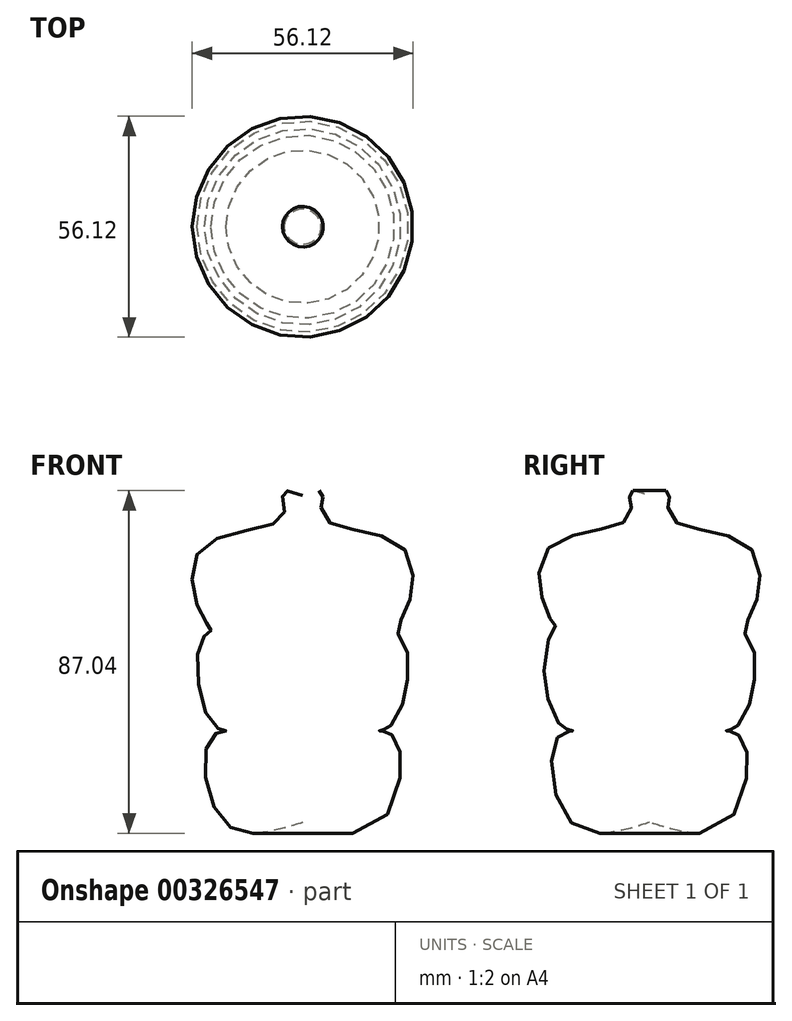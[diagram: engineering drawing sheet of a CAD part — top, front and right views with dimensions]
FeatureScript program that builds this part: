
annotation { "Feature Type Name" : "Feature", "Feature Type Description" : "" }
export const myFeature = defineFeature(function(context is Context, id is Id, definition is map)
    precondition{}
    {
        {
            var Q0;
            Q0=qCreatedBy(makeId("Front.planeOp"),FACE);
            var sketch = newSketch(context, id + "F0", { "sketchPlane" : qUnion([Q0])});
            skLineSegment(sketch, "E0", {"start": v(0, -31.14) * mm, "end": v(0, 51.9) * mm, "construction": true});
            skFitSpline(sketch, "E1", {"points": [v(0, -31.14) * mm, v(-19.91, -31.14) * mm, v(-23.3, -9.53) * mm, v(-19.5, -7.84) * mm, v(-22.88, -6.14) * mm, v(-25.85, 15.04) * mm, v(-23.3, 17.58) * mm, v(-25.42, 20.97) * mm, v(-25.42, 38.77) * mm, v(-5.08, 46.4) * mm, v(-5.08, 52.75) * mm, v(0, 51.9) * mm], "startDerivative": vector(-180.87, -56.26) * mm, "endDerivative": vector(108.12, -41.86) * mm});
            skLineSegment(sketch, "E2", {"start": v(0, 51.9) * mm, "end": v(0, -31.14) * mm});
            skSolve(sketch);
        }
        {
            var Q0;
            Q0=makeQuery(id+"F0.imprint","IMPRINT",FACE,{"disambiguationData":[TD([[makeQuery(id+"F0.imprint","IMPRINT",EDGE,{"derivedFrom":sQuery(id+"F0.wireOp",EDGE,"E1")}),-1.0]])]});
            var Q1;
            Q1=sQuery(id+"F0.wireOp",EDGE,"E2");
            revolve(context, id + "F1", {"entities" : qUnion([Q0]), "axis" : qUnion([Q1]), "revolveType" : RevolveType.FULL});
        }
    });
